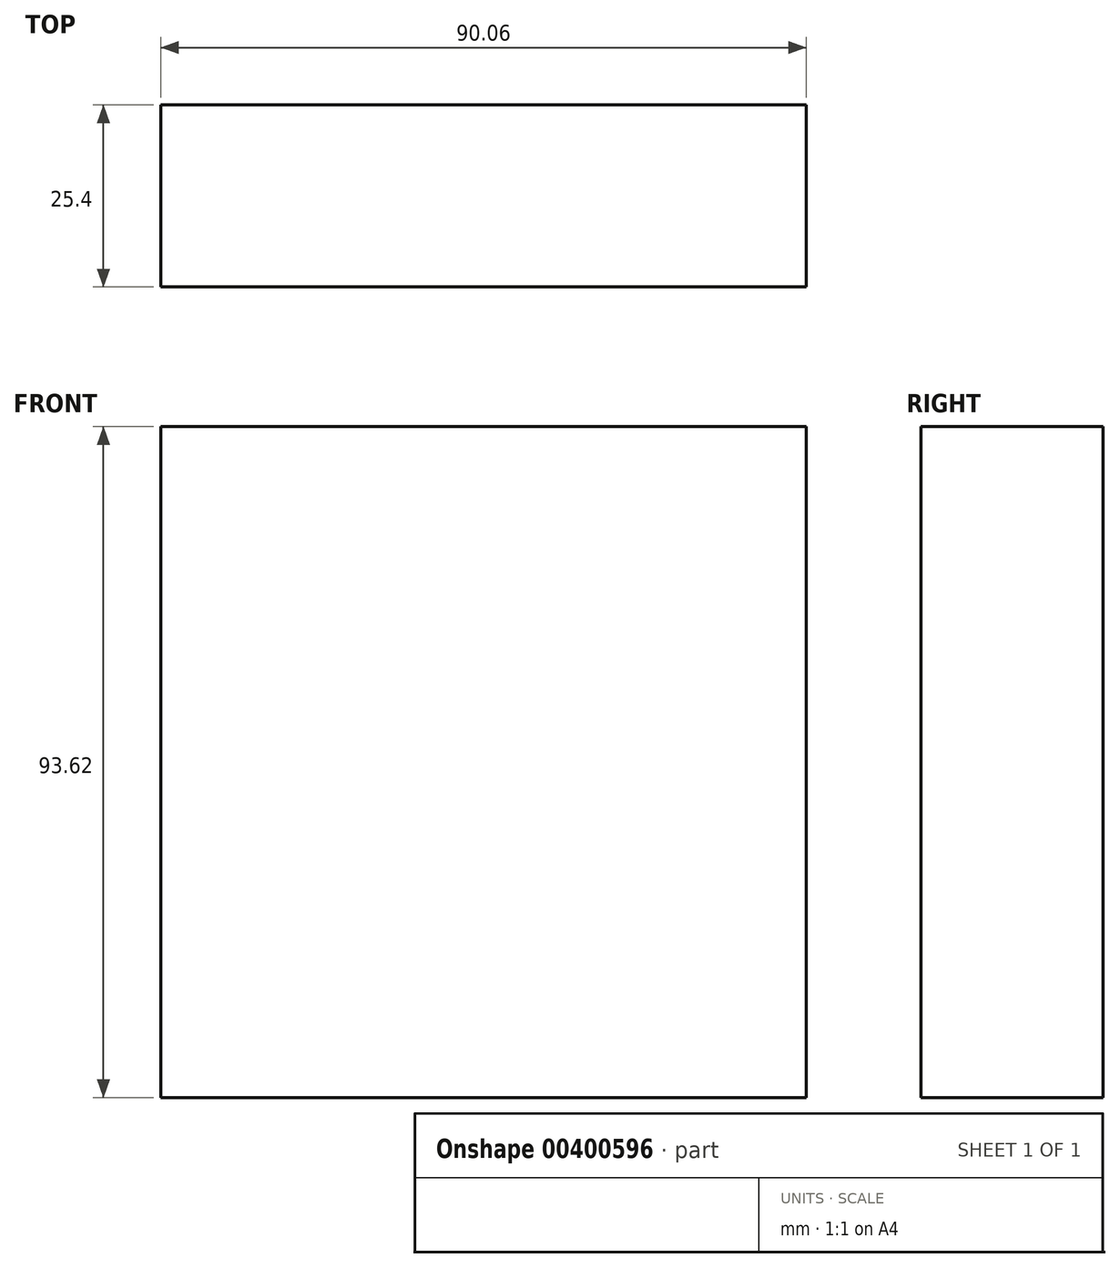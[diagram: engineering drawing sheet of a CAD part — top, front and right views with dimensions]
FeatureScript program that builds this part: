
annotation { "Feature Type Name" : "Feature", "Feature Type Description" : "" }
export const myFeature = defineFeature(function(context is Context, id is Id, definition is map)
    precondition{}
    {
        {
            var Q0;
            Q0=qCreatedBy(makeId("Front.planeOp"),FACE);
            var sketch = newSketch(context, id + "F0", { "sketchPlane" : qUnion([Q0])});
            skLineSegment(sketch, "E0.bottom", {"start": v(-45.03, 46.81) * mm, "end": v(45.03, 46.81) * mm});
            skLineSegment(sketch, "E0.top", {"start": v(-45.03, -46.81) * mm, "end": v(45.03, -46.81) * mm});
            skLineSegment(sketch, "E0.left", {"start": v(-45.03, 46.81) * mm, "end": v(-45.03, -46.81) * mm});
            skLineSegment(sketch, "E0.right", {"start": v(45.03, 46.81) * mm, "end": v(45.03, -46.81) * mm});
            skPoint(sketch, "E0.middle", {"position": v(0, 0) * mm});
            skSolve(sketch);
        }
        {
            var Q0;
            Q0 = qSketchRegion(id + "F0", true);
            extrude(context, id + "F1", {"entities" : qUnion([Q0]), "depth" : 25.4 * mm});
        }
    });
